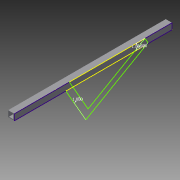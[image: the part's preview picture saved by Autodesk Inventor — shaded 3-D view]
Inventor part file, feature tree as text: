
AUTODESK INVENTOR PART (.ipt)
format: ipt  version: 2013 (Build 170138000, 138)  size: 83,968 bytes
history: native  units: in
note: dims shown in document units (in); Inventor stores cm internally (conversion verified against a paired STEP export)
features: sketch x2, extrude x1
ambient origin geometry x8: Origin, YZ Plane, XZ Plane, XY Plane, X Axis, Y Axis, Z Axis, Center Point
bodies: Solid1 (feature_tree)
feature tree (3):
  extrude  "Extrusion1"  Depth=1.0in
  sketch  "Sketch2"  dims[d3=0.125in d4=26.0in d5=0.0in d6=1.0in d9=1.0in d12=1.0in]
  sketch  "Sketch1"  dims[d0=1.0in d2=1.0in]
